# Revit family: Accessory-Bundle-KOHLER-Bento-K-35000
name_source: partatom
category: Specialty Equipment
units: mm (PartAtom-declared; Revit-internal decimal feet)

## family parameters
Cut with Voids When Loaded = No
Host = Face
OmniClass Number = 23.31.25.00
OmniClass Title = Toilet and Bath Specialties
Part Type = Normal
Room Calculation Point = No
Round Connector Dimension = Use Diameter
Shared = No

## types (2) — shared parameters
ADA Compliant = No
Assembly Code = C1030200
Date Modified = 07/23/2024
Default Elevation = 0"
Description = Core Bundle Accessories - Bevel
Height = 4 3/8"
Length = 17"
Manufacturer = Kohler Co.
Master Format 2014 = 10 28 00
Master Format 2014 Name = Toilet, Bath, and Laundry Accessories
Material = Plastic
Product Documentation Link = https://www.us.kohler.com
Product Name = Bento
Product Page URL = http://www.us.kohler.com
URL = https://www.us.kohler.com
WaterSense Certified = No

## per-type parameters (varying)
| type | Colander Finish | Drying Rack Finish | Finish | Model | Soaking Bin Finish | Type |
| DRK | Kohler-Plastic-2DK-Dark | Kohler-Plastic-1DK-Dark | Kohler-Plastic-1DK-Dark | K-35000-DRK | Kohler-Plastic-3DK-Dark | 1 |
| LGT | Kohler-Plastic-2LG-Light | Kohler-Plastic-1LG-Light | Kohler-Plastic-1LG-Light | K-35000-LGT | Kohler-Plastic-3LG-Light | 2 |

## geometry (parser evidence)
native form markers: Sweep x8
no freeform markers — native parametric forms only
